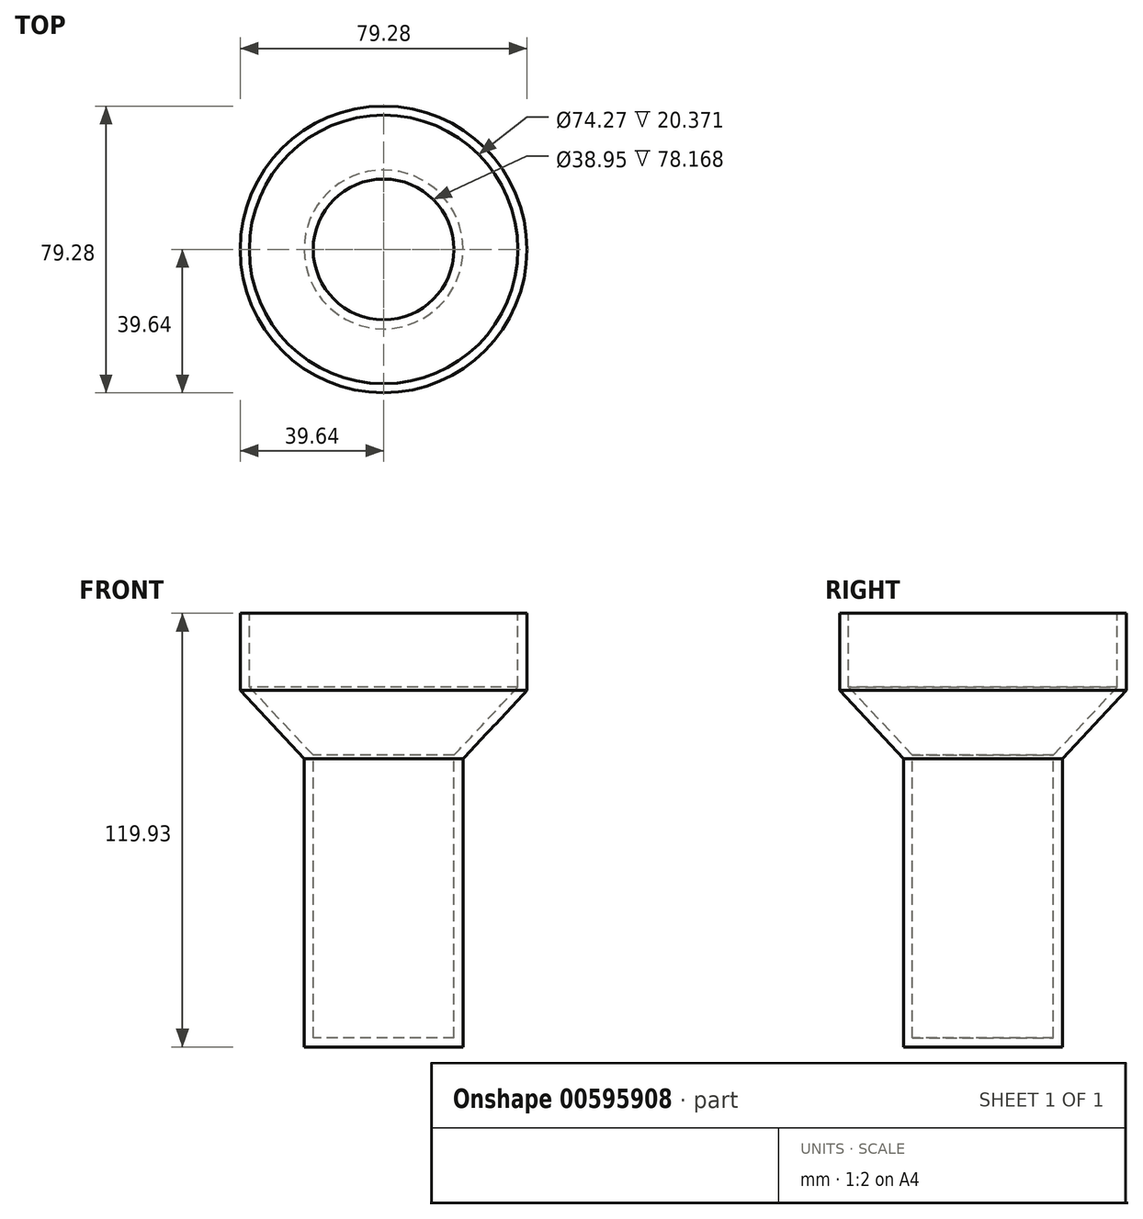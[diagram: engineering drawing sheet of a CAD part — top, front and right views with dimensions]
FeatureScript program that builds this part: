
annotation { "Feature Type Name" : "Feature", "Feature Type Description" : "" }
export const myFeature = defineFeature(function(context is Context, id is Id, definition is map)
    precondition{}
    {
        {
            var Q0;
            Q0=qCreatedBy(makeId("Right.planeOp"),FACE);
            var sketch = newSketch(context, id + "F0", { "sketchPlane" : qUnion([Q0])});
            skLineSegment(sketch, "E0", {"start": v(0, -59.76) * mm, "end": v(-21.97, -59.76) * mm});
            skLineSegment(sketch, "E1", {"start": v(-21.97, -59.76) * mm, "end": v(-21.97, 19.92) * mm});
            skLineSegment(sketch, "E2", {"start": v(-21.97, 19.92) * mm, "end": v(-39.64, 38.81) * mm});
            skLineSegment(sketch, "E3", {"start": v(-39.64, 38.81) * mm, "end": v(-39.64, 60.17) * mm});
            skLineSegment(sketch, "E4", {"start": v(-39.64, 60.17) * mm, "end": v(0, 60.17) * mm});
            skLineSegment(sketch, "E5", {"start": v(0, 60.17) * mm, "end": v(0, -59.76) * mm});
            skSolve(sketch);
        }
        {
            var Q0;
            Q0=makeQuery(id+"F0.imprint","IMPRINT",FACE,{"disambiguationData":[TD([[makeQuery(id+"F0.imprint","IMPRINT",EDGE,{"derivedFrom":sQuery(id+"F0.wireOp",EDGE,"E0")}),-1.0]])]});
            var Q1;
            Q1=sQuery(id+"F0.wireOp",EDGE,"E5");
            revolve(context, id + "F1", {"entities" : qUnion([Q0]), "axis" : qUnion([Q1]), "revolveType" : RevolveType.FULL});
        }
        {
            var Q0;
            Q0=makeQuery(id+"F1.opRevolve","SWEPT_FACE",FACE,{"disambiguationData":[OSD([sQuery(id+"F0.wireOp",EDGE,"E4")])]});
            shell(context, id + "F2", {"entities" : qUnion([Q0]), "thickness" : 2.5 * mm});
        }
    });
